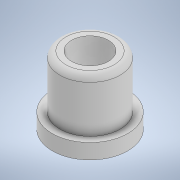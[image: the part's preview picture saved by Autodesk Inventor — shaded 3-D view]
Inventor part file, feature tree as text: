
AUTODESK INVENTOR PART (.ipt)
format: ipt  version: 2022 (Build 260153000, 153)  size: 131,072 bytes
history: native  units: mm
features: extrude x3, sketch x3, fillet x1
ambient origin geometry x8: Origin, YZ Plane, XZ Plane, XY Plane, X Axis, Y Axis, Z Axis, Center Point
bodies: Solid1 (feature_tree)
feature tree (7):
  extrude  "Extrusion1"  Depth=22.5mm TaperAngle=0.0deg
  extrude  "Extrusion2"  TaperAngle=0.0deg  [1 undecoded]
  extrude  "Extrusion3"  Depth=5.0mm TaperAngle=0.0deg
  fillet  "Fillet1"  Radius=2.0mm
  sketch  "Sketch1"  dims[d0=20.0mm d1=22.5mm d2=0.0mm]
  sketch  "Sketch2"  dims[d3=12.2mm d4=0.0mm d5=0.0mm]
  sketch  "Sketch3"  dims[d6=25.0mm d7=5.0mm d8=0.0mm d9=2.0mm]
note: 1 required parameter value undecoded (feature->parameter linkage not recoverable at this tier; creation-order binding heuristic only, values carry confidence <= 0.55)
